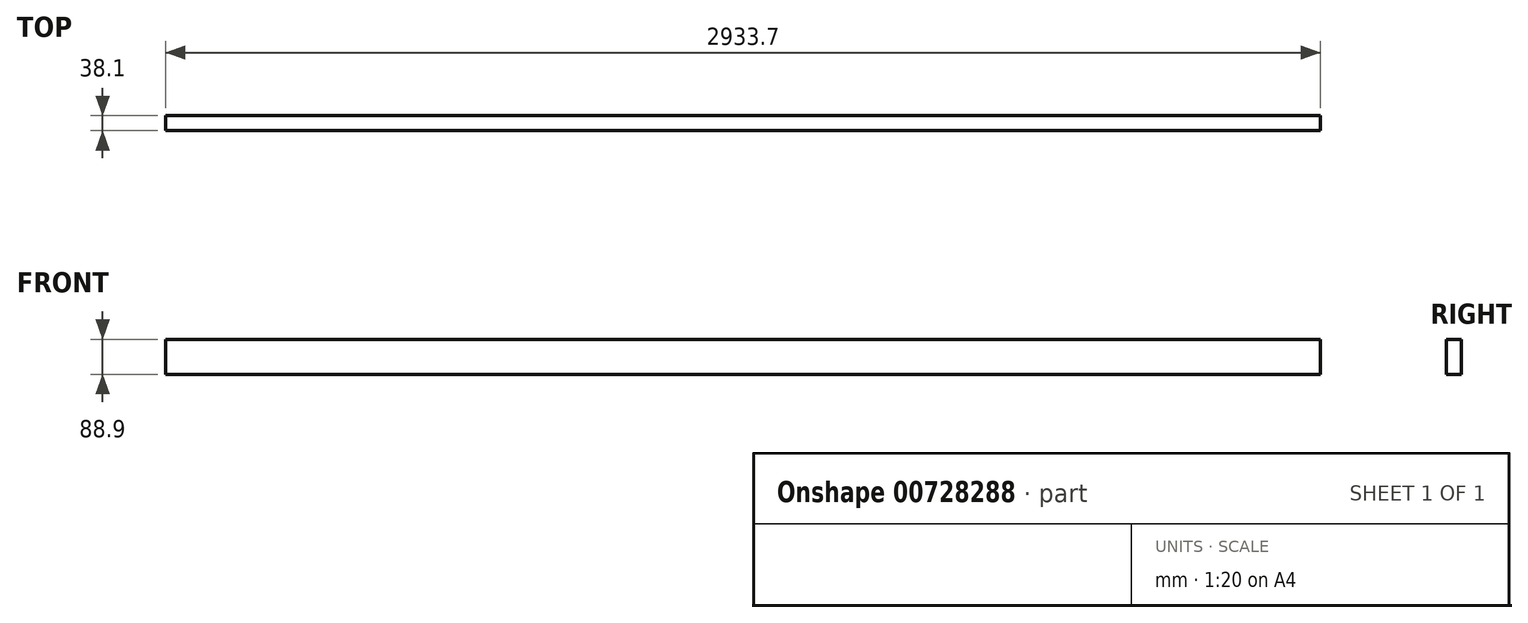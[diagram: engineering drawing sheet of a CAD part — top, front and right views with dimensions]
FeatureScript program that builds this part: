
annotation { "Feature Type Name" : "Feature", "Feature Type Description" : "" }
export const myFeature = defineFeature(function(context is Context, id is Id, definition is map)
    precondition{}
    {
        {
            var Q0;
            Q0=qCreatedBy(makeId("Front.planeOp"),FACE);
            var sketch = newSketch(context, id + "F0", { "sketchPlane" : qUnion([Q0])});
            skLineSegment(sketch, "E0.bottom", {"start": v(-1466.85, -44.45) * mm, "end": v(1466.85, -44.45) * mm});
            skLineSegment(sketch, "E0.top", {"start": v(-1466.85, 44.45) * mm, "end": v(1466.85, 44.45) * mm});
            skLineSegment(sketch, "E0.left", {"start": v(-1466.85, -44.45) * mm, "end": v(-1466.85, 44.45) * mm});
            skLineSegment(sketch, "E0.right", {"start": v(1466.85, -44.45) * mm, "end": v(1466.85, 44.45) * mm});
            skPoint(sketch, "E0.middle", {"position": v(0, 0) * mm});
            skSolve(sketch);
        }
        {
            var Q0;
            Q0=qSketchRegion(id+"F0",true);
            extrude(context, id + "F1", {"entities" : qUnion([Q0]), "depth" : 38.1 * mm, "offsetDistance" : 25.4 * mm});
        }
    });
